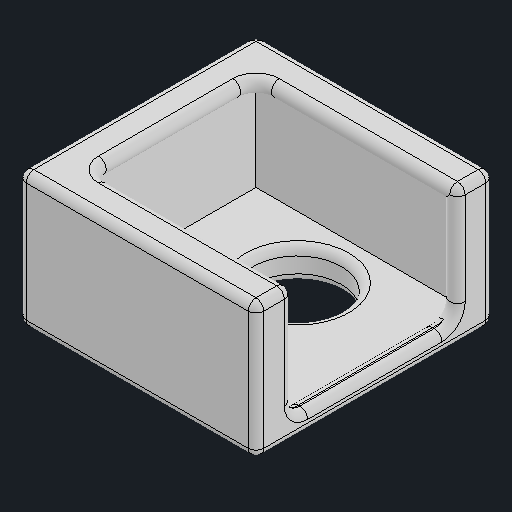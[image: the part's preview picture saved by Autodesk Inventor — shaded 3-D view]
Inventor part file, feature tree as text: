
AUTODESK INVENTOR PART (.ipt)
format: ipt  version: 2024.2 (Build 282272000, 272)  size: 182,784 bytes
history: native  units: mm
features: other x1, fillet x1
ambient origin geometry x8: Origin, YZ Plane, XZ Plane, XY Plane, X Axis, Y Axis, Z Axis, Center Point
bodies: Body1 (feature_tree)
feature tree (2):
  other  "솔리드1"
  fillet  "Fillet2"  [1 undecoded]
note: 1 required parameter value undecoded (feature->parameter linkage not recoverable at this tier; creation-order binding heuristic only, values carry confidence <= 0.55)
